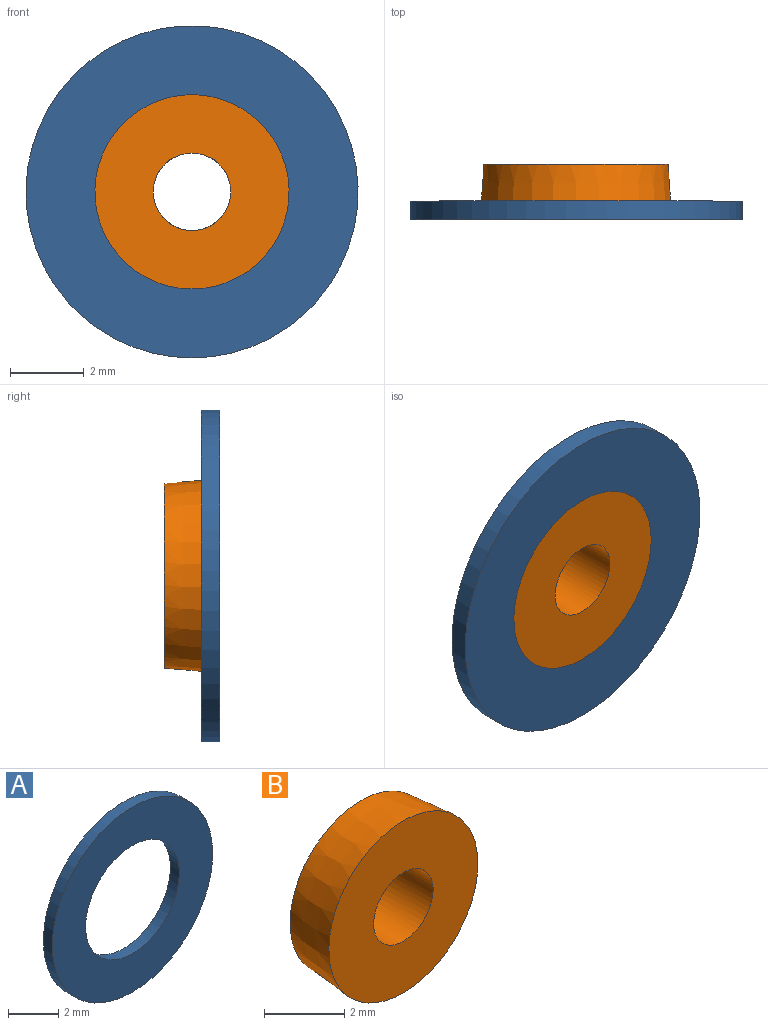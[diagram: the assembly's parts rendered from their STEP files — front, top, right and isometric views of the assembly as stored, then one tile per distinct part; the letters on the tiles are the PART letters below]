
ASSEMBLY  parts=2 mates=1
PART A: 4 faces, bbox 9x0.5x9 mm
  f0: cylinder r=2.63mm len=5.26mm, axis (0,-1,0), area 8.3mm2, adj f2,f3
  f1: cylinder r=4.5mm len=9mm, axis (0,-1,0), area 14.1mm2, adj f2,f3
  f2: plane 9x9mm, normal (0,1,0), area 41.9mm2, adj f0,f1
  f3: plane 9x9mm, normal (0,-1,0), area 41.9mm2, adj f0,f1
PART B: 10 faces, bbox 5.3x1.5x5.3 mm
  f0: plane 3.1x3.1mm, normal (0,1,0), area 4.1mm2, adj f4,f7
  f1: cone r=2.5mm half-angle=5deg, axis (0,-1,0), area 24.3mm2, adj f2,f3
  f2: plane 5.26x5.26mm, normal (0,-1,0), area 18.3mm2, adj f1,f4
  f3: plane 5x5mm, normal (0,1,0), area 7.1mm2, adj f1,f5
  f4: cylinder r=1.05mm len=2.1mm, axis (0,1,0), area 9.9mm2, adj f0,f2
  f5: cone r=2mm half-angle=5deg, axis (0,-1,0), area 12.9mm2, adj f3,f6
  f6: plane 4.17x4.17mm, normal (0,1,0), area 1.2mm2, adj f5,f8
  f7: cylinder r=1.55mm len=3.1mm, axis (0,1,0), area 1.9mm2, adj f0,f9
  f8: cylinder r=1.99mm len=3.99mm, axis (0,-1,0), area 10mm2, adj f6,f9
  f9: plane 3.99x3.99mm, normal (0,1,0), area 5mm2, adj f7,f8
PLACE A t=(-0.71,1.07,0.25)mm
PLACE B t=(-0.71,1.07,0.25)mm
MATE fastened B.f1 <-> A.f0  axis (0,-1,0) through (-0.71,-0.43,0.25)mm
